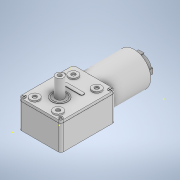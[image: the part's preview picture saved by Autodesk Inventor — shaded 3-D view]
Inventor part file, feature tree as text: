
AUTODESK INVENTOR PART (.ipt)
format: ipt  version: 2021 (Build 250183000, 183)  size: 429,056 bytes
history: native  units: mm
features: sketch x25, extrude x22, fillet x6, other x1
ambient origin geometry x8: Origin, YZ Plane, XZ Plane, XY Plane, X Axis, Y Axis, Z Axis, Center Point
bodies: Body1 (feature_tree)
feature tree (54):
  other  "Sólido1"
  extrude  "Extrusión1"  Depth=31.5mm
  extrude  "Extrusión2"  Depth=33.0mm TaperAngle=0.0deg
  sketch  "Boceto3"  dims[d15=6.0mm d16=0.0mm d17=2.0mm]
  extrude  "Extrusión3"  Depth=2.0mm
  extrude  "Extrusión4"  Depth=1.0mm TaperAngle=0.0deg
  extrude  "Extrusión5"  Depth=3.0mm
  extrude  "Extrusión6"  Depth=4.0mm TaperAngle=0.0deg
  extrude  "Extrusión7"  Depth=3.0mm TaperAngle=0.0deg
  extrude  "Extrusión8"  Depth=2.0mm TaperAngle=0.0deg
  extrude  "Extrusión9"  Depth=2.0mm
  sketch  "Boceto11"  dims[d95=2.0mm d96=0.0mm d97=0.1mm]
  fillet  "Empalme1"  Radius=2.0mm
  fillet  "Empalme2"  Radius=2.0mm
  fillet  "Empalme3"  Radius=2.0mm
  fillet  "Empalme4"  Radius=2.0mm
  fillet  "Empalme5"  Radius=2.0mm
  extrude  "Extrusión10"  Depth=2.0mm TaperAngle=0.0deg
  extrude  "Extrusión11"  Depth=0.1mm
  extrude  "Extrusión12"  Depth=2.0mm TaperAngle=0.0deg
  extrude  "Extrusión13"  Depth=10.0mm
  sketch  "Boceto16"  dims[d132=0.4mm d133=0.0mm d134=0.123mm]
  extrude  "Extrusión14"  Depth=0.3mm TaperAngle=0.0deg
  extrude  "Extrusión15"  Depth=13.0mm TaperAngle=0.0deg
  extrude  "Extrusión16"  Depth=0.123mm
  extrude  "Extrusión17"  Depth=0.05mm TaperAngle=0.0deg
  extrude  "Extrusión18"  [1 undecoded]
  extrude  "Extrusión19"  [1 undecoded]
  extrude  "Extrusión20"  [1 undecoded]
  fillet  "Empalme6"  [1 undecoded]
  extrude  "Extrusión21"  [1 undecoded]
  extrude  "Extrusión22"  [1 undecoded]
  sketch  "Boceto1"  dims[d0=41.0mm d1=31.5mm]
  sketch  "Boceto2"  dims[d2=21.0mm d3=0.0mm d11=33.0mm d12=0.0mm]
  sketch  "Boceto4"  dims[d18=1.0mm d19=0.0mm d26=5.0mm d27=0.0mm]
  sketch  "Boceto5"  dims[d30=4.0mm d31=3.0mm]
  sketch  "Boceto6"  dims[d32=4.0mm d33=4.0mm d34=0.0mm]
  sketch  "Boceto7"  dims[d35=1.0mm d49=3.0mm d50=0.0mm]
  sketch  "Boceto8"  dims[d63=5.5mm d64=0.0mm d69=2.0mm d70=0.0mm]
  sketch  "Boceto9"  dims[d71=2.0mm d72=2.0mm d73=2.0mm d74=2.0mm d75=2.0mm d87=2.0mm d88=0.0mm d89=2.0mm]
  sketch  "Boceto10"  dims[d91=2.0mm d92=0.0mm d93=2.0mm d94=0.0mm]
  sketch  "Boceto12"  dims[d98=2.0mm d99=0.0mm d100=2.0mm d101=0.0mm]
  sketch  "Boceto13"  dims[d106=0.3mm d107=0.0mm d110=10.0mm]
  sketch  "Boceto14"  dims[d111=9.9mm d112=0.3mm d113=0.0mm]
  sketch  "Boceto15"  dims[d115=14.0mm d116=0.0mm d118=13.0mm d119=0.0mm]
  sketch  "Boceto17"  dims[d149=0.05mm d150=0.0mm d167=0.05mm d168=0.0mm]
  sketch  "Boceto18"  dims[d90=0.872665mm]
  sketch  "Boceto19"
  sketch  "Boceto20"
  sketch  "Boceto21"
  sketch  "Boceto22"
  sketch  "Boceto23"
  sketch  "Boceto24"
  sketch  "Boceto26"
note: 6 required parameter values undecoded (feature->parameter linkage not recoverable at this tier; creation-order binding heuristic only, values carry confidence <= 0.55)
